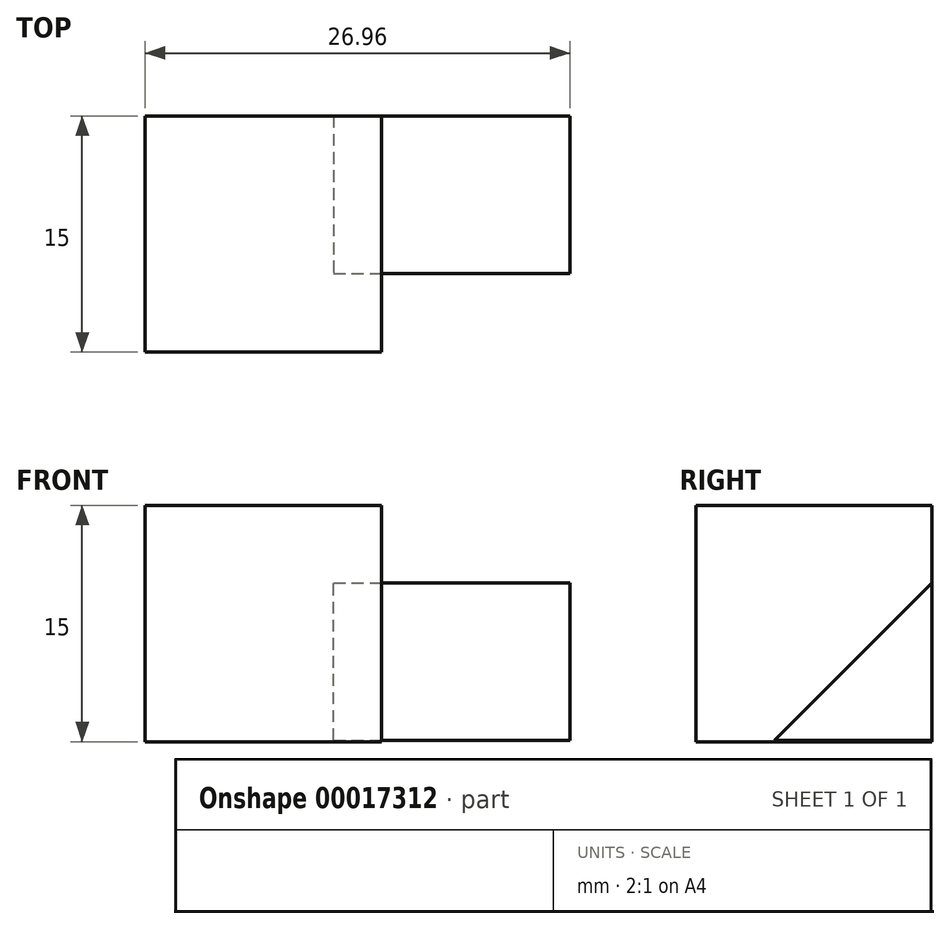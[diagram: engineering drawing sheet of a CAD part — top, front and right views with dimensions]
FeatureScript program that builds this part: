
annotation { "Feature Type Name" : "Feature", "Feature Type Description" : "" }
export const myFeature = defineFeature(function(context is Context, id is Id, definition is map)
    precondition{}
    {
        {
            var Q0;
            Q0=qCreatedBy(makeId("Front.planeOp"),FACE);
            var sketch = newSketch(context, id + "F0", { "sketchPlane" : qUnion([Q0])});
            skLineSegment(sketch, "E0", {"start": v(-26.96, 19.9) * mm, "end": v(-11.96, 19.9) * mm});
            skLineSegment(sketch, "E1", {"start": v(-11.96, 19.9) * mm, "end": v(-11.96, 4.9) * mm});
            skLineSegment(sketch, "E2", {"start": v(-11.96, 4.9) * mm, "end": v(-26.96, 4.9) * mm});
            skLineSegment(sketch, "E3", {"start": v(-26.96, 4.9) * mm, "end": v(-26.96, 19.9) * mm});
            skSolve(sketch);
        }
        {
            var Q0;
            Q0=makeQuery(id+"F0.imprint","IMPRINT",FACE,{"disambiguationData":[TD([[makeQuery(id+"F0.imprint","IMPRINT",EDGE,{"derivedFrom":sQuery(id+"F0.wireOp",EDGE,"E0")}),-1.0]])]});
            extrude(context, id + "F1", {"entities" : qUnion([Q0]), "depth" : 15 * mm});
        }
        {
            var Q0;
            Q0=qCreatedBy(makeId("Right.planeOp"),FACE);
            var sketch = newSketch(context, id + "F2", { "sketchPlane" : qUnion([Q0])});
            skLineSegment(sketch, "E4", {"start": v(0, 15) * mm, "end": v(-10, 5) * mm});
            skLineSegment(sketch, "E5", {"start": v(-10, 5) * mm, "end": v(0, 5) * mm});
            skLineSegment(sketch, "E6", {"start": v(0, 5) * mm, "end": v(0, 15) * mm});
            skSolve(sketch);
        }
        {
            var Q0;
            Q0=makeQuery(id+"F2.imprint","IMPRINT",FACE,{"disambiguationData":[TD([[makeQuery(id+"F2.imprint","IMPRINT",EDGE,{"derivedFrom":sQuery(id+"F2.wireOp",EDGE,"E4")}),1.0]])]});
            extrude(context, id + "F3", {"entities" : qUnion([Q0]), "oppositeDirection" : true, "depth" : 15 * mm});
        }
    });
